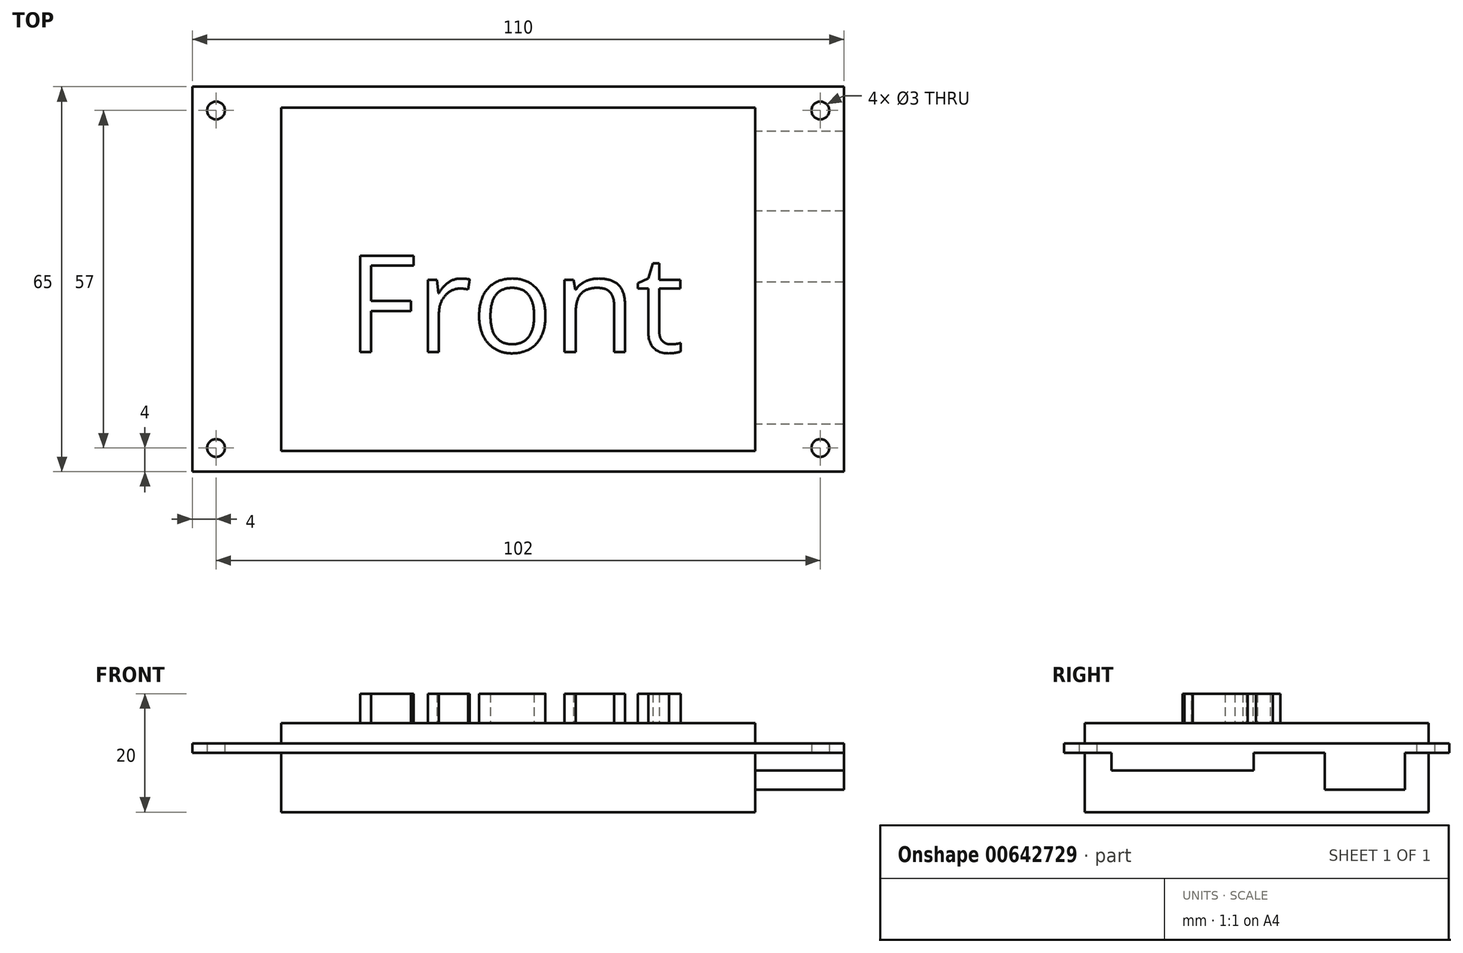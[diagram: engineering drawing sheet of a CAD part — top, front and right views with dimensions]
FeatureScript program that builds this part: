
annotation { "Feature Type Name" : "Feature", "Feature Type Description" : "" }
export const myFeature = defineFeature(function(context is Context, id is Id, definition is map)
    precondition{}
    {
        {
            var Q0;
            Q0=qCreatedBy(makeId("Top.planeOp"),FACE);
            var sketch = newSketch(context, id + "F0", { "sketchPlane" : qUnion([Q0])});
            skLineSegment(sketch, "E0.bottom", {"start": v(-55, 28.4) * mm, "end": v(55, 28.4) * mm});
            skLineSegment(sketch, "E0.top", {"start": v(-55, -36.6) * mm, "end": v(55, -36.6) * mm});
            skLineSegment(sketch, "E0.left", {"start": v(-55, 28.4) * mm, "end": v(-55, -36.6) * mm});
            skLineSegment(sketch, "E0.right", {"start": v(55, 28.4) * mm, "end": v(55, -36.6) * mm});
            skCircle(sketch, "E1", {"center": v(-51, -32.6) * mm, "radius": 1.5 * mm});
            skCircle(sketch, "E2.0.1.0", {"center": v(-51, 24.4) * mm, "radius": 1.5 * mm});
            skCircle(sketch, "E2.1.0.0", {"center": v(51, -32.6) * mm, "radius": 1.5 * mm});
            skCircle(sketch, "E2.1.1.0", {"center": v(51, 24.4) * mm, "radius": 1.5 * mm});
            skLineSegment(sketch, "E2.direction1", {"start": v(-51, -32.6) * mm, "end": v(51, -32.6) * mm, "construction": true});
            skLineSegment(sketch, "E2.direction2", {"start": v(-51, -32.6) * mm, "end": v(-51, 24.4) * mm, "construction": true});
            skLineSegment(sketch, "E3.bottom", {"start": v(40, 24.9) * mm, "end": v(-40, 24.9) * mm});
            skLineSegment(sketch, "E3.top", {"start": v(40, -33.1) * mm, "end": v(-40, -33.1) * mm});
            skLineSegment(sketch, "E3.left", {"start": v(40, 24.9) * mm, "end": v(40, -33.1) * mm});
            skLineSegment(sketch, "E3.right", {"start": v(-40, 24.9) * mm, "end": v(-40, -33.1) * mm});
            skPoint(sketch, "E3.middle", {"position": v(0, -4.1) * mm});
            skSolve(sketch);
        }
        {
            var Q0;
            {var subQ1=sQuery(id+"F0.wireOp",EDGE,"E0.bottom");Q0=makeQuery(id+"F0.imprint","IMPRINT",FACE,{"disambiguationData":[TD([[makeQuery(id+"F0.imprint","IMPRINT",EDGE,{"derivedFrom":subQ1}),-1.0]])]});}
            extrude(context, id + "F1", {"entities" : qUnion([Q0]), "depth" : 1.6 * mm, "offsetDistance" : 25 * mm});
        }
        {
            var Q0;
            Q0=makeQuery(id+"F0.imprint","IMPRINT",FACE,{"disambiguationData":[TD([[makeQuery(id+"F0.imprint","IMPRINT",EDGE,{"derivedFrom":sQuery(id+"F0.wireOp",EDGE,"E3.bottom")}),1.0]])]});
            extrude(context, id + "F2", {"entities" : qUnion([Q0]), "operationType" : NewBodyOperationType.ADD, "depth" : 5 * mm, "offsetDistance" : 25 * mm});
        }
        {
            var Q0;
            Q0=makeQuery(id+"F0.imprint","IMPRINT",FACE,{"disambiguationData":[TD([[makeQuery(id+"F0.imprint","IMPRINT",EDGE,{"derivedFrom":sQuery(id+"F0.wireOp",EDGE,"E3.bottom")}),1.0]])]});
            extrude(context, id + "F3", {"entities" : qUnion([Q0]), "operationType" : NewBodyOperationType.ADD, "oppositeDirection" : true, "depth" : 10 * mm, "offsetDistance" : 25 * mm});
        }
        {
            var Q0;
            Q0=makeQuery(id+"F2.opExtrude","CAP_FACE",FACE,{"disambiguationData":[OSD([sQuery(id+"F0.wireOp",EDGE,"E3.bottom"),sQuery(id+"F0.wireOp",EDGE,"E3.top"),sQuery(id+"F0.wireOp",EDGE,"E3.left"),sQuery(id+"F0.wireOp",EDGE,"E3.right")])],"isStart":false});
            var sketch = newSketch(context, id + "F4", { "sketchPlane" : qUnion([Q0])});
            skText(sketch, "E4", { "text": "Front", "fontName": "OpenSans-Regular.ttf"});
            const initialGuessF4  = {"E4": [-0.02893, -0.0164, 1, 0, 0.0164]};
            skSetInitialGuess(sketch, initialGuessF4);
            skSolve(sketch);
        }
        {
            var Q0;
            Q0=makeQuery(id+"F4.imprint","IMPRINT",FACE,{"disambiguationData":[TD([[makeQuery(id+"F4.imprint","IMPRINT",EDGE,{"derivedFrom":sQuery(id+"F4.wireOp",EDGE,"E4.sketch_text.stroke-0")}),-1.0]])]});
            var Q1;
            Q1=makeQuery(id+"F4.imprint","IMPRINT",FACE,{"disambiguationData":[TD([[makeQuery(id+"F4.imprint","IMPRINT",EDGE,{"derivedFrom":sQuery(id+"F4.wireOp",EDGE,"E4.sketch_text.stroke-10")}),-1.0]])]});
            var Q2;
            Q2=makeQuery(id+"F4.imprint","IMPRINT",FACE,{"disambiguationData":[TD([[makeQuery(id+"F4.imprint","IMPRINT",EDGE,{"derivedFrom":sQuery(id+"F4.wireOp",EDGE,"E4.sketch_text.stroke-23")}),-1.0]])]});
            var Q3;
            Q3=makeQuery(id+"F4.imprint","IMPRINT",FACE,{"disambiguationData":[TD([[makeQuery(id+"F4.imprint","IMPRINT",EDGE,{"derivedFrom":sQuery(id+"F4.wireOp",EDGE,"E4.sketch_text.stroke-40")}),-1.0]])]});
            var Q4;
            Q4=makeQuery(id+"F4.imprint","IMPRINT",FACE,{"disambiguationData":[TD([[makeQuery(id+"F4.imprint","IMPRINT",EDGE,{"derivedFrom":sQuery(id+"F4.wireOp",EDGE,"E4.sketch_text.stroke-57")}),-1.0]])]});
            extrude(context, id + "F5", {"entities" : qUnion([Q0, Q1, Q2, Q3, Q4]), "operationType" : NewBodyOperationType.ADD, "depth" : 5 * mm, "offsetDistance" : 25 * mm});
        }
        {
            var Q0;
            Q0=makeQuery(id+"F0.imprint","IMPRINT",FACE,{"disambiguationData":[TD([[makeQuery(id+"F0.imprint","IMPRINT",EDGE,{"derivedFrom":sQuery(id+"F0.wireOp",EDGE,"E0.bottom")}),-1.0]])]});
            var sketch = newSketch(context, id + "F6", { "sketchPlane" : qUnion([Q0])});
            skLineSegment(sketch, "E5.bottom", {"start": v(55, 20.9) * mm, "end": v(37.4, 20.9) * mm});
            skLineSegment(sketch, "E5.top", {"start": v(55, 7.4) * mm, "end": v(37.4, 7.4) * mm});
            skLineSegment(sketch, "E5.left", {"start": v(55, 20.9) * mm, "end": v(55, 7.4) * mm});
            skLineSegment(sketch, "E5.right", {"start": v(37.4, 20.9) * mm, "end": v(37.4, 7.4) * mm});
            skLineSegment(sketch, "E6.bottom", {"start": v(55, -28.6) * mm, "end": v(32.76, -28.6) * mm});
            skLineSegment(sketch, "E6.top", {"start": v(55, -4.6) * mm, "end": v(32.76, -4.6) * mm});
            skLineSegment(sketch, "E6.left", {"start": v(55, -28.6) * mm, "end": v(55, -4.6) * mm});
            skLineSegment(sketch, "E6.right", {"start": v(32.76, -28.6) * mm, "end": v(32.76, -4.6) * mm});
            skSolve(sketch);
        }
        {
            var Q0;
            {var subQ0=sQuery(id+"F6.wireOp",EDGE,"E5.left");Q0=makeQuery(id+"F6.imprint","IMPRINT",FACE,{"disambiguationData":[TD([[makeQuery(id+"F6.imprint","IMPRINT",EDGE,{"derivedFrom":subQ0}),-1.0]])]});}
            extrude(context, id + "F7", {"entities" : qUnion([Q0]), "operationType" : NewBodyOperationType.ADD, "oppositeDirection" : true, "depth" : 6.2 * mm, "offsetDistance" : 25 * mm});
        }
        {
            var Q0;
            {var subQ0=sQuery(id+"F6.wireOp",EDGE,"E6.left");Q0=makeQuery(id+"F6.imprint","IMPRINT",FACE,{"disambiguationData":[TD([[makeQuery(id+"F6.imprint","IMPRINT",EDGE,{"derivedFrom":subQ0}),-1.0]])]});}
            extrude(context, id + "F8", {"entities" : qUnion([Q0]), "operationType" : NewBodyOperationType.ADD, "oppositeDirection" : true, "depth" : 3 * mm, "offsetDistance" : 25 * mm});
        }
    });
